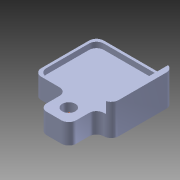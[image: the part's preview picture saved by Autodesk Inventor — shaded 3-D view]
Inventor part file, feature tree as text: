
AUTODESK INVENTOR PART (.ipt)
format: ipt  version: 2011 (Build 150239000, 239)  size: 146,944 bytes
history: native  units: in
note: dims shown in document units (in); Inventor stores cm internally (conversion verified against a paired STEP export)
features: sketch x2, other x1, imported_body x1, extrude x1
ambient origin geometry x8: Origin, YZ Plane, XZ Plane, XY Plane, X Axis, Y Axis, Z Axis, Center Point
feature tree (5):
  other  "rectangle_lid_D"
  imported_body  "Base1"
  sketch  "Sketch1"  dims[d0=0.1378in d1=0.3937in d2=0.0in]
  extrude  "Extrusion1"  Depth=0.3937in TaperAngle=0.0deg
  sketch  "Sketch2"
